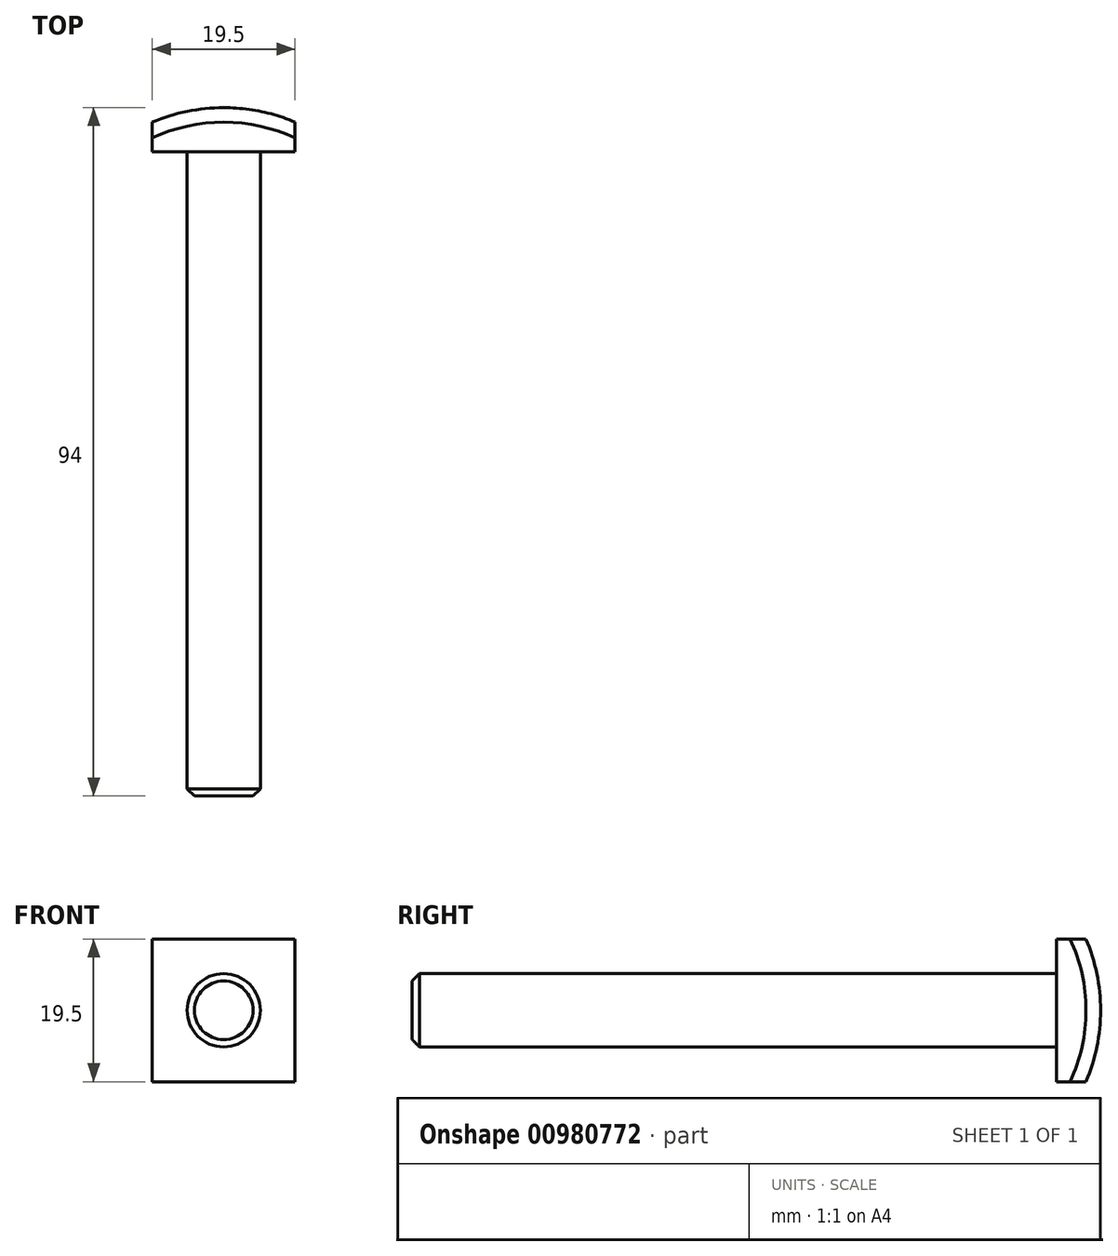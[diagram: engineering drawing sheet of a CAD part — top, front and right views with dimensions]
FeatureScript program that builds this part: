
annotation { "Feature Type Name" : "Feature", "Feature Type Description" : "" }
export const myFeature = defineFeature(function(context is Context, id is Id, definition is map)
    precondition{}
    {
        {
            var Q0;
            Q0=qCreatedBy(makeId("Front.planeOp"),FACE);
            var sketch = newSketch(context, id + "F0", { "sketchPlane" : qUnion([Q0])});
            skLineSegment(sketch, "E0.bottom", {"start": v(9.75, 9.75) * mm, "end": v(-9.75, 9.75) * mm});
            skLineSegment(sketch, "E0.top", {"start": v(9.75, -9.75) * mm, "end": v(-9.75, -9.75) * mm});
            skLineSegment(sketch, "E0.left", {"start": v(9.75, 9.75) * mm, "end": v(9.75, -9.75) * mm});
            skLineSegment(sketch, "E0.right", {"start": v(-9.75, 9.75) * mm, "end": v(-9.75, -9.75) * mm});
            skPoint(sketch, "E0.middle", {"position": v(0, 0) * mm});
            skLineSegment(sketch, "E1", {"start": v(-9.75, 9.75) * mm, "end": v(9.75, -9.75) * mm, "construction": true});
            skLineSegment(sketch, "E2", {"start": v(9.75, 9.75) * mm, "end": v(-9.75, -9.75) * mm, "construction": true});
            skSolve(sketch);
        }
        {
            var Q0;
            Q0 = qSketchRegion(id + "F0", true);
            extrude(context, id + "F1", {"entities" : qUnion([Q0]), "depth" : 6 * mm, "offsetDistance" : 25 * mm});
        }
        {
            var Q0;
            Q0=makeQuery(id+"F1.opExtrude","CAP_FACE",FACE,{"disambiguationData":[OSD([sQuery(id+"F0.wireOp",EDGE,"E0.bottom"),sQuery(id+"F0.wireOp",EDGE,"E0.top"),sQuery(id+"F0.wireOp",EDGE,"E0.left"),sQuery(id+"F0.wireOp",EDGE,"E0.right")])],"isStart":false});
            var sketch = newSketch(context, id + "F2", { "sketchPlane" : qUnion([Q0])});
            skCircle(sketch, "E3", {"center": v(0, 0) * mm, "radius": 5 * mm});
            skSolve(sketch);
        }
        {
            var Q0;
            Q0 = qSketchRegion(id + "F2", true);
            extrude(context, id + "F3", {"entities" : qUnion([Q0]), "operationType" : NewBodyOperationType.ADD, "depth" : 88 * mm, "offsetDistance" : 25 * mm});
        }
        {
            var Q0;
            Q0=makeQuery(id+"F3.opExtrude","CAP_FACE",FACE,{"disambiguationData":[OSD([sQuery(id+"F2.wireOp",EDGE,"E3")])],"isStart":false});
            chamfer(context, id + "F4", {"entities" : qUnion([Q0]), "width" : 1 * mm, "tangentPropagation" : true});
        }
        {
            var Q0;
            Q0=qCreatedBy(makeId("Top.planeOp"),FACE);
            var sketch = newSketch(context, id + "F5", { "sketchPlane" : qUnion([Q0])});
            skArc(sketch, "E4", {"start": v(25, -25) * mm, "mid": v(17.68, -7.32) * mm, "end": v(0, 0) * mm});
            skArc(sketch, "E5", {"start": v(35.53, -25) * mm, "mid": v(25.12, 0.12) * mm, "end": v(0, 10.53) * mm});
            skLineSegment(sketch, "E6", {"start": v(0, 10.53) * mm, "end": v(0, 0) * mm});
            skLineSegment(sketch, "E7", {"start": v(25, -25) * mm, "end": v(35.53, -25) * mm});
            skSolve(sketch);
        }
        {
            var Q0;
            Q0 = qSketchRegion(id + "F5", true);
            var Q1;
            Q1=sQuery(id+"F5.wireOp",EDGE,"E6");
            revolve(context, id + "F6", {"operationType" : NewBodyOperationType.REMOVE, "surfaceOperationType" : NewSurfaceOperationType.NEW, "entities" : qUnion([Q0]), "axis" : qUnion([Q1]), "revolveType" : RevolveType.FULL, "oppositeDirection" : true});
        }
    });
